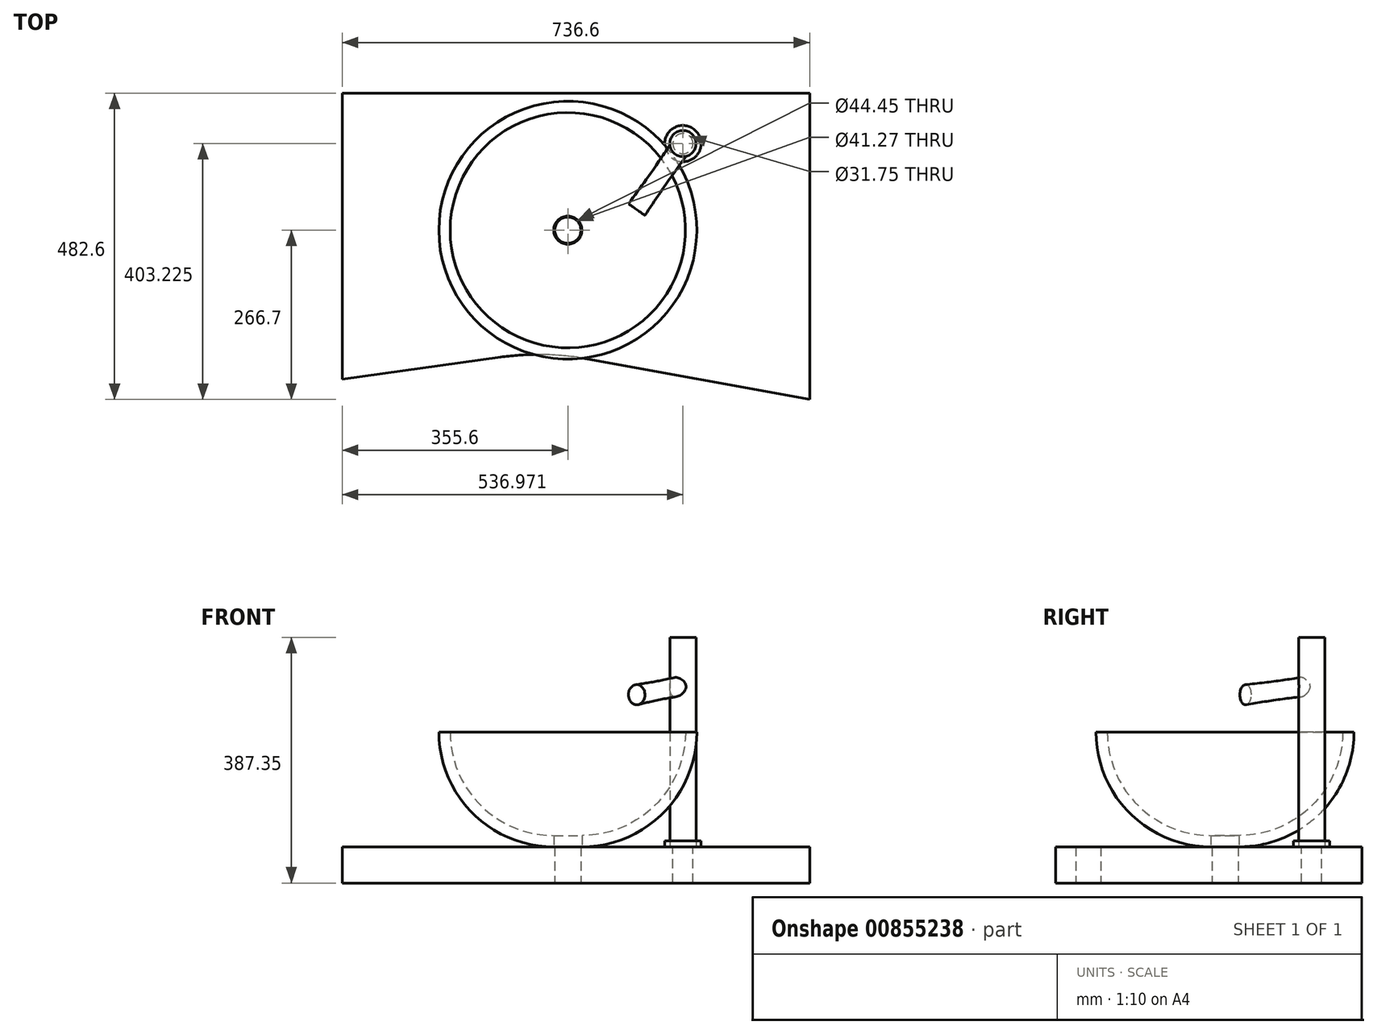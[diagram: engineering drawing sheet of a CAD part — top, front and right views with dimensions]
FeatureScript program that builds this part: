
annotation { "Feature Type Name" : "Feature", "Feature Type Description" : "" }
export const myFeature = defineFeature(function(context is Context, id is Id, definition is map)
    precondition{}
    {
        {
            var Q0;
            Q0=qCreatedBy(makeId("Top.planeOp"),FACE);
            var sketch = newSketch(context, id + "F0", { "sketchPlane" : qUnion([Q0])});
            skLineSegment(sketch, "E0.bottom", {"start": v(-368.3, 241.3) * mm, "end": v(368.3, 241.3) * mm});
            skLineSegment(sketch, "E0.top", {"start": v(-368.3, -241.3) * mm, "end": v(368.3, -241.3) * mm, "construction": true});
            skLineSegment(sketch, "E0.left", {"start": v(-368.3, 241.3) * mm, "end": v(-368.3, -241.3) * mm});
            skLineSegment(sketch, "E0.right", {"start": v(368.3, 241.3) * mm, "end": v(368.3, -241.3) * mm});
            skPoint(sketch, "E0.middle", {"position": v(0, 0) * mm});
            skCircle(sketch, "E1", {"center": v(-12.7, 25.4) * mm, "radius": 20.64 * mm});
            skLineSegment(sketch, "E2", {"start": v(368.3, -241.3) * mm, "end": v(18.46, -177.55) * mm});
            skLineSegment(sketch, "E3", {"start": v(-118.64, -174.7) * mm, "end": v(-368.3, -209.55) * mm});
            skPoint(sketch, "E4.visualSharp", {"position": v(-49.86, -165.1) * mm});
            skArc(sketch, "E4.filletArc", {"start": v(18.46, -177.55) * mm, "mid": v(-49.98, -170.65) * mm, "end": v(-118.64, -174.7) * mm});
            skSolve(sketch);
        }
        {
            var Q0;
            Q0 = qSketchRegion(id + "F0", true);
            extrude(context, id + "F1", {"entities" : qUnion([Q0]), "depth" : 57.15 * mm, "offsetDistance" : 25.4 * mm});
        }
        {
            var Q0;
            Q0=makeQuery(id+"F1.opExtrude","SWEPT_FACE",FACE,{"disambiguationData":[OSD([sQuery(id+"F0.wireOp",EDGE,"E1")])]});
            cPlane(context, id + "F2", {"entities" : qUnion([Q0]), "cplaneType" : CPlaneType.LINE_ANGLE, "offset" : 25.4 * mm, "angle" : 90 * degree, "width" : 152.4 * mm, "height" : 152.4 * mm});
        }
        {
            var Q0;
            Q0=qCreatedBy(id+"F2.planeOp",FACE);
            var sketch = newSketch(context, id + "F3", { "sketchPlane" : qUnion([Q0])});
            skLineSegment(sketch, "E5", {"start": v(12.7, 57.15) * mm, "end": v(12.7, 209.55) * mm, "construction": true});
            skLineSegment(sketch, "E6", {"start": v(-9.52, 57.15) * mm, "end": v(-9.52, 74.93) * mm});
            skArc(sketch, "E7", {"start": v(-190.5, 238.12) * mm, "mid": v(-137.5, 110.16) * mm, "end": v(-9.52, 57.15) * mm});
            skArc(sketch, "E8.0", {"start": v(-172.72, 238.13) * mm, "mid": v(-124.92, 122.73) * mm, "end": v(-9.52, 74.93) * mm});
            skLineSegment(sketch, "E9", {"start": v(-172.72, 238.13) * mm, "end": v(-190.5, 238.13) * mm});
            skSolve(sketch);
        }
        {
            var Q0;
            Q0 = qSketchRegion(id + "F3", true);
            var Q1;
            Q1=sQuery(id+"F3.wireOp",EDGE,"E5");
            revolve(context, id + "F4", {"surfaceOperationType" : NewSurfaceOperationType.NEW, "entities" : qUnion([Q0]), "axis" : qUnion([Q1]), "revolveType" : RevolveType.FULL});
        }
        {
            var Q0;
            Q0=makeQuery(id+"F1.opExtrude","CAP_FACE",FACE,{"disambiguationData":[OSD([sQuery(id+"F0.wireOp",EDGE,"E0.bottom"),sQuery(id+"F0.wireOp",EDGE,"E0.left"),sQuery(id+"F0.wireOp",EDGE,"E0.right"),sQuery(id+"F0.wireOp",EDGE,"E1"),sQuery(id+"F0.wireOp",EDGE,"E2"),sQuery(id+"F0.wireOp",EDGE,"llintMWl-BFjs-GZYb-sYE1-h0Uw6EXNfp59"),sQuery(id+"F0.wireOp",EDGE,"acaba12e-47c0-4c51-8041-441ab46a32d9.filletArc")])],"isStart":false});
            var sketch = newSketch(context, id + "F5", { "sketchPlane" : qUnion([Q0])});
            skCircle(sketch, "E10", {"center": v(168.67, 161.92) * mm, "radius": 15.88 * mm});
            skCircle(sketch, "E11", {"center": v(-12.7, 25.4) * mm, "radius": 87.31 * mm, "construction": true});
            skCircle(sketch, "E12.0", {"center": v(-12.7, 25.4) * mm, "radius": 203.2 * mm, "construction": true});
            skLineSegment(sketch, "E13", {"start": v(-12.7, 25.4) * mm, "end": v(168.67, 161.92) * mm, "construction": true});
            skSolve(sketch);
        }
        {
            var Q0;
            Q0 = qSketchRegion(id + "F5", true);
            extrude(context, id + "F6", {"entities" : qUnion([Q0]), "operationType" : NewBodyOperationType.REMOVE, "endBound" : BoundingType.THROUGH_ALL, "oppositeDirection" : true, "depth" : 25.4 * mm, "offsetDistance" : 25.4 * mm});
        }
        {
            var Q0;
            Q0=makeQuery(id+"F1.opExtrude","CAP_FACE",FACE,{"disambiguationData":[OSD([sQuery(id+"F0.wireOp",EDGE,"E0.bottom"),sQuery(id+"F0.wireOp",EDGE,"E0.left"),sQuery(id+"F0.wireOp",EDGE,"E0.right"),sQuery(id+"F0.wireOp",EDGE,"E1"),sQuery(id+"F0.wireOp",EDGE,"E2"),sQuery(id+"F0.wireOp",EDGE,"llintMWl-BFjs-GZYb-sYE1-h0Uw6EXNfp59"),sQuery(id+"F0.wireOp",EDGE,"acaba12e-47c0-4c51-8041-441ab46a32d9.filletArc")])],"isStart":false});
            var sketch = newSketch(context, id + "F7", { "sketchPlane" : qUnion([Q0])});
            skCircle(sketch, "E14", {"center": v(168.67, 161.92) * mm, "radius": 28.58 * mm});
            skSolve(sketch);
        }
        {
            var Q0;
            Q0 = qSketchRegion(id + "F7", true);
            extrude(context, id + "F8", {"entities" : qUnion([Q0]), "depth" : 9.52 * mm, "offsetDistance" : 25.4 * mm});
        }
        {
            var Q0;
            Q0=makeQuery(id+"F1.opExtrude","CAP_FACE",FACE,{"disambiguationData":[OSD([sQuery(id+"F0.wireOp",EDGE,"E0.bottom"),sQuery(id+"F0.wireOp",EDGE,"E0.left"),sQuery(id+"F0.wireOp",EDGE,"E0.right"),sQuery(id+"F0.wireOp",EDGE,"E1"),sQuery(id+"F0.wireOp",EDGE,"E2"),sQuery(id+"F0.wireOp",EDGE,"llintMWl-BFjs-GZYb-sYE1-h0Uw6EXNfp59"),sQuery(id+"F0.wireOp",EDGE,"acaba12e-47c0-4c51-8041-441ab46a32d9.filletArc")])],"isStart":false});
            var sketch = newSketch(context, id + "F9", { "sketchPlane" : qUnion([Q0])});
            skCircle(sketch, "E15", {"center": v(168.67, 161.92) * mm, "radius": 20.64 * mm});
            skSolve(sketch);
        }
        {
            var Q0;
            Q0 = qSketchRegion(id + "F9", true);
            extrude(context, id + "F10", {"entities" : qUnion([Q0]), "depth" : 330.2 * mm, "offsetDistance" : 25.4 * mm});
        }
        {
            var Q0;
            Q0=makeQuery(id+"F10.opExtrude","SWEPT_FACE",FACE,{"disambiguationData":[OSD([sQuery(id+"F9.wireOp",EDGE,"E15")])]});
            cPlane(context, id + "F11", {"entities" : qUnion([Q0]), "cplaneType" : CPlaneType.LINE_ANGLE, "offset" : 25.4 * mm, "angle" : 125 * degree, "width" : 152.4 * mm, "height" : 152.4 * mm});
        }
        {
            var Q0;
            Q0=qCreatedBy(id+"F11.planeOp",FACE);
            var sketch = newSketch(context, id + "F12", { "sketchPlane" : qUnion([Q0])});
            skCircle(sketch, "E16", {"center": v(-45.3, 311.15) * mm, "radius": 15.88 * mm});
            skLineSegment(sketch, "E17", {"start": v(-45.3, 387.35) * mm, "end": v(-45.3, 311.15) * mm});
            skSolve(sketch);
        }
        {
            var Q0;
            Q0=qCreatedBy(id+"F11.planeOp",FACE);
            cPlane(context, id + "F13", {"entities" : qUnion([Q0]), "cplaneType" : CPlaneType.OFFSET, "offset" : 127 * mm, "oppositeDirection" : true, "width" : 152.4 * mm, "height" : 152.4 * mm});
        }
        {
            var Q0;
            Q0=qCreatedBy(id+"F13.planeOp",FACE);
            var sketch = newSketch(context, id + "F14", { "sketchPlane" : qUnion([Q0])});
            skCircle(sketch, "E18", {"center": v(-45.3, 296.86) * mm, "radius": 15.88 * mm});
            skSolve(sketch);
        }
        {
            var Q1;
            Q1=makeQuery(id+"F14.imprint","IMPRINT",FACE,{"disambiguationData":[TD([[makeQuery(id+"F14.imprint","IMPRINT",EDGE,{"derivedFrom":sQuery(id+"F14.wireOp",EDGE,"E18")}),1.0]])]});
            var Q2;
            Q2 = qSketchRegion(id + "F12", true);
            loft(context, id + "F15", {"operationType" : NewBodyOperationType.ADD, "sheetProfilesArray" : [{ "sheetProfileEntities" : qUnion([Q1]) }, { "sheetProfileEntities" : qUnion([Q2]) }]});
        }
    });
